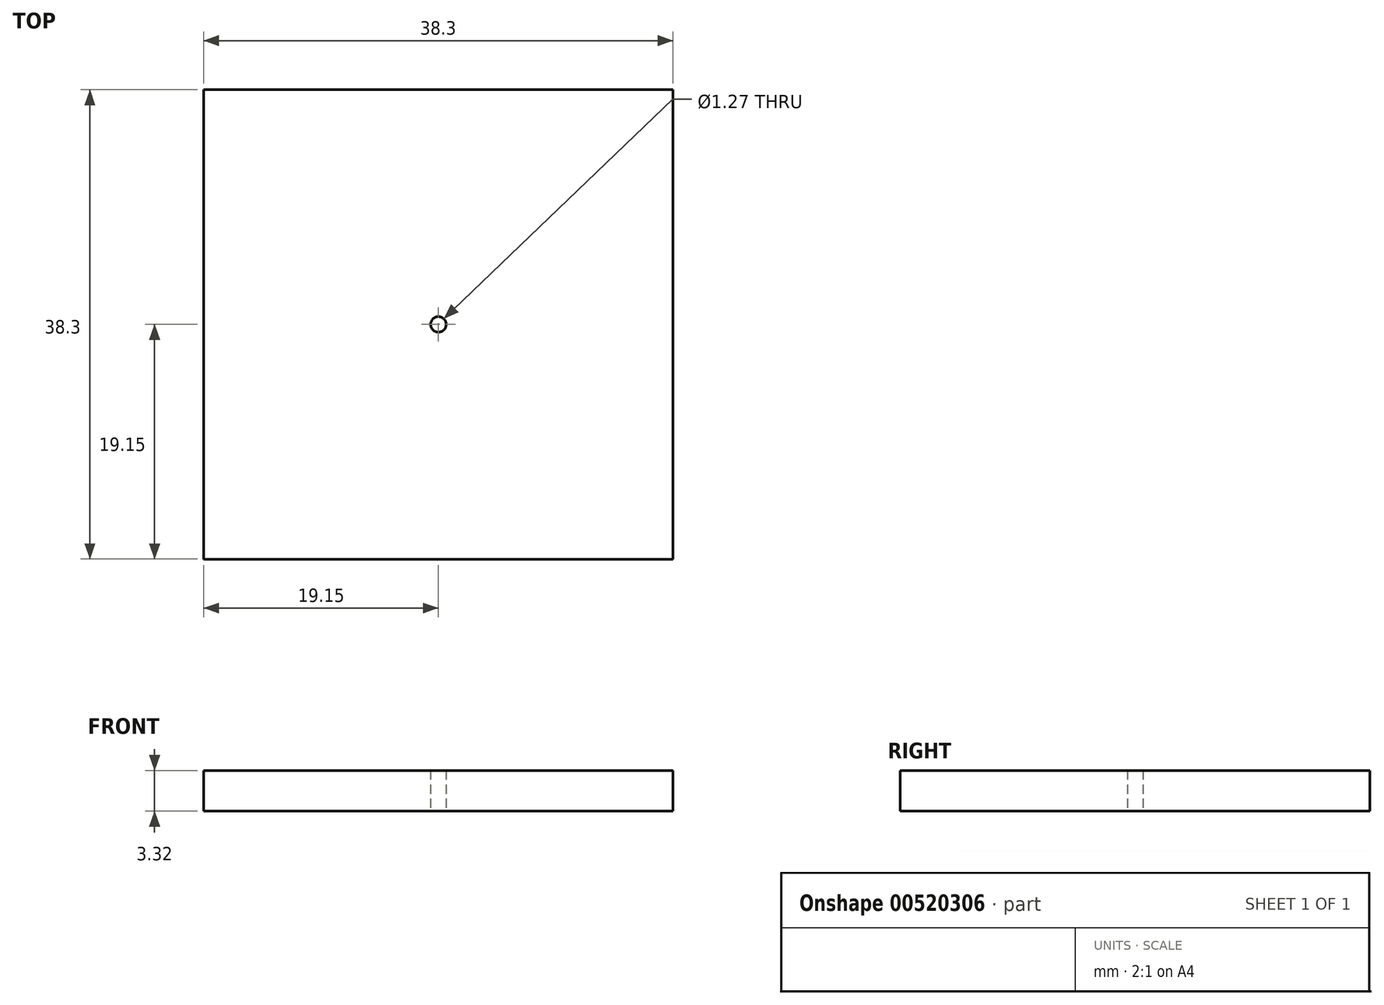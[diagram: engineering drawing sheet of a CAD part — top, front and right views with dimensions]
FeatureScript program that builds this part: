
annotation { "Feature Type Name" : "Feature", "Feature Type Description" : "" }
export const myFeature = defineFeature(function(context is Context, id is Id, definition is map)
    precondition{}
    {
        {
            var Q0;
            Q0=qCreatedBy(makeId("Front.planeOp"),FACE);
            var sketch = newSketch(context, id + "F0", { "sketchPlane" : qUnion([Q0])});
            skLineSegment(sketch, "E0.bottom", {"start": v(19.15, -1.66) * mm, "end": v(-19.15, -1.66) * mm});
            skLineSegment(sketch, "E0.top", {"start": v(19.15, 1.66) * mm, "end": v(-19.15, 1.66) * mm});
            skLineSegment(sketch, "E0.left", {"start": v(19.15, -1.66) * mm, "end": v(19.15, 1.66) * mm});
            skLineSegment(sketch, "E0.right", {"start": v(-19.15, -1.66) * mm, "end": v(-19.15, 1.66) * mm});
            skPoint(sketch, "E0.middle", {"position": v(0, 0) * mm});
            skSolve(sketch);
        }
        {
            var Q0;
            Q0 = qSketchRegion(id + "F0", true);
            extrude(context, id + "F1", {"entities" : qUnion([Q0]), "depth" : 38.3 * mm, "offsetDistance" : 25.4 * mm});
        }
        {
            var Q0;
            Q0=makeQuery(id+"F1.opExtrude","SWEPT_BODY",BODY,{"disambiguationData":[OSD([sQuery(id+"F0.wireOp",EDGE,"E0.bottom"),sQuery(id+"F0.wireOp",EDGE,"E0.top"),sQuery(id+"F0.wireOp",EDGE,"E0.left"),sQuery(id+"F0.wireOp",EDGE,"E0.right")])]});
            var Q1;
            Q1=makeQuery(id+"F1.opExtrude","CAP_FACE",FACE,{"disambiguationData":[OSD([sQuery(id+"F0.wireOp",EDGE,"E0.bottom"),sQuery(id+"F0.wireOp",EDGE,"E0.top"),sQuery(id+"F0.wireOp",EDGE,"E0.left"),sQuery(id+"F0.wireOp",EDGE,"E0.right")])],"isStart":true});
            transform(context, id + "F2", {"entities" : qUnion([Q0]), "transformType" : TransformType.TRANSLATION_DISTANCE, "transformDirection" : qUnion([Q1]), "distance" : 19.15 * mm, "makeCopy" : false});
        }
        {
            var Q0;
            Q0=makeQuery(id+"F1.opExtrude","SWEPT_FACE",FACE,{"disambiguationData":[OSD([sQuery(id+"F0.wireOp",EDGE,"E0.bottom")])]});
            var sketch = newSketch(context, id + "F3", { "sketchPlane" : qUnion([Q0])});
            skPoint(sketch, "E1", {"position": v(0, 0) * mm});
            skSolve(sketch);
        }
        {
            var Q0;
            Q0=sQuery(id+"F3.wireOp",VERTEX,"E1");
            var Q1;
            Q1=makeQuery(id+"F1.opExtrude","SWEPT_BODY",BODY,{"disambiguationData":[OSD([sQuery(id+"F0.wireOp",EDGE,"E0.bottom"),sQuery(id+"F0.wireOp",EDGE,"E0.top"),sQuery(id+"F0.wireOp",EDGE,"E0.left"),sQuery(id+"F0.wireOp",EDGE,"E0.right")])]});
            hole(context, id + "F4", {"style" : HoleStyle.SIMPLE, "endStyle" : HoleEndStyle.THROUGH, "holeDiameter" : 1.27 * mm, "isTappedThrough" : true, "tappedDepth" : 12.7 * mm, "tapClearance" : 3, "locations" : qUnion([Q0]), "scope" : qUnion([Q1])});
        }
    });
